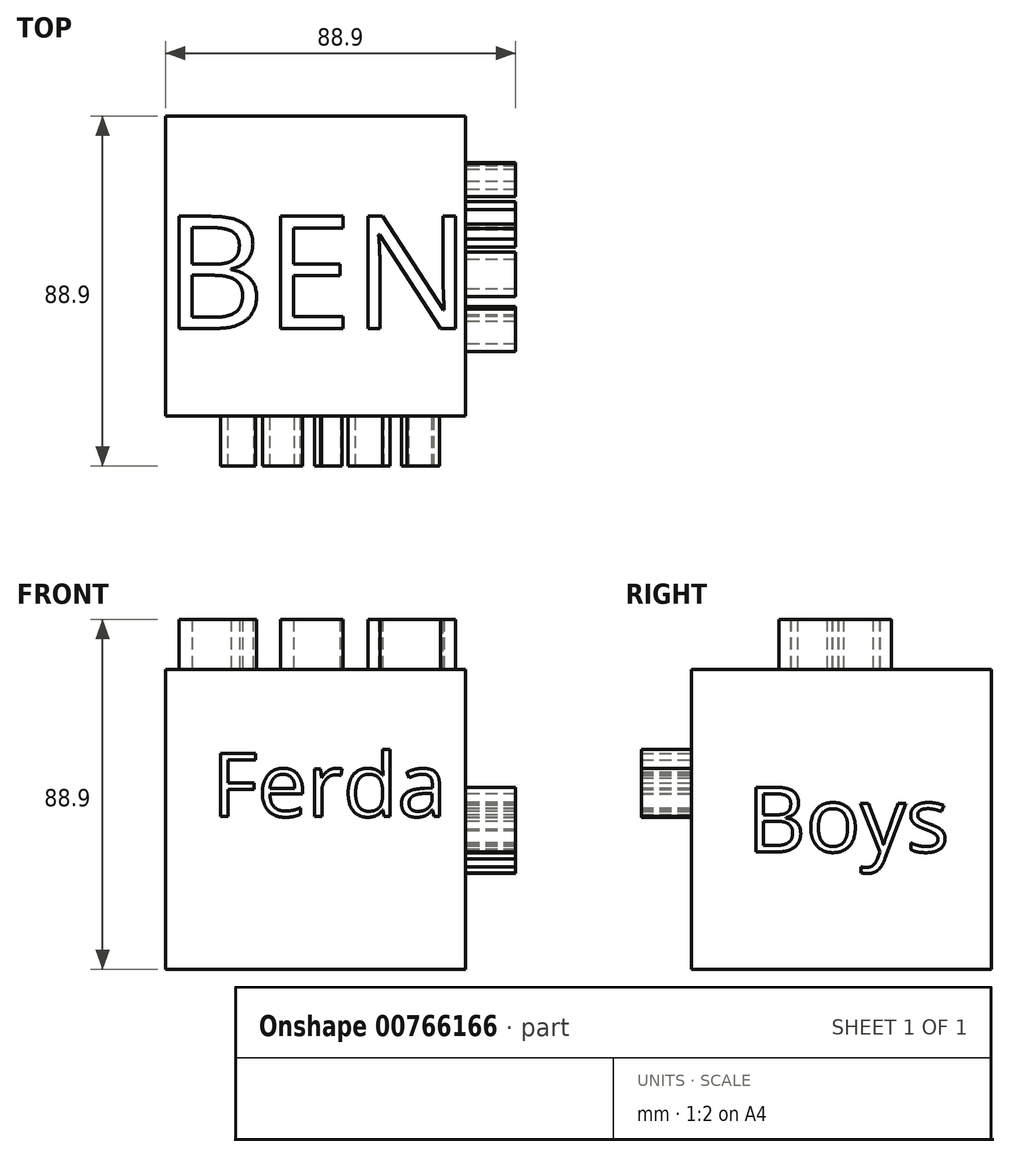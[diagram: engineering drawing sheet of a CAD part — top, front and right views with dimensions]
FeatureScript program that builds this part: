
annotation { "Feature Type Name" : "Feature", "Feature Type Description" : "" }
export const myFeature = defineFeature(function(context is Context, id is Id, definition is map)
    precondition{}
    {
        {
            var Q0;
            Q0=qCreatedBy(makeId("Front.planeOp"),FACE);
            var sketch = newSketch(context, id + "F0", { "sketchPlane" : qUnion([Q0])});
            skLineSegment(sketch, "E0.bottom", {"start": v(-41.32, 48.96) * mm, "end": v(34.88, 48.96) * mm});
            skLineSegment(sketch, "E0.top", {"start": v(-41.32, -27.24) * mm, "end": v(34.88, -27.24) * mm});
            skLineSegment(sketch, "E0.left", {"start": v(-41.32, 48.96) * mm, "end": v(-41.32, -27.24) * mm});
            skLineSegment(sketch, "E0.right", {"start": v(34.88, 48.96) * mm, "end": v(34.88, -27.24) * mm});
            skSolve(sketch);
        }
        {
            var Q0;
            Q0 = qSketchRegion(id + "F0", true);
            extrude(context, id + "F1", {"entities" : qUnion([Q0]), "depth" : 76.2 * mm, "offsetDistance" : 25.4 * mm});
        }
        {
            var Q0;
            Q0=makeQuery(id+"F1.opExtrude","SWEPT_FACE",FACE,{"disambiguationData":[OSD([sQuery(id+"F0.wireOp",EDGE,"E0.bottom")])]});
            var sketch = newSketch(context, id + "F2", { "sketchPlane" : qUnion([Q0])});
            skText(sketch, "E1", { "text": "BEN", "fontName": "OpenSans-Regular.ttf"});
            const initialGuessF2  = {"E1": [-0.04184, -0.05392, 1, 0, 0.0287]};
            skSetInitialGuess(sketch, initialGuessF2);
            skSolve(sketch);
        }
        {
            var Q0;
            Q0 = qSketchRegion(id + "F2", true);
            extrude(context, id + "F3", {"entities" : qUnion([Q0]), "operationType" : NewBodyOperationType.ADD, "depth" : 12.7 * mm, "offsetDistance" : 25.4 * mm});
        }
        {
            var Q0;
            Q0=makeQuery(id+"F1.opExtrude","CAP_FACE",FACE,{"disambiguationData":[OSD([sQuery(id+"F0.wireOp",EDGE,"E0.bottom"),sQuery(id+"F0.wireOp",EDGE,"E0.top"),sQuery(id+"F0.wireOp",EDGE,"E0.left"),sQuery(id+"F0.wireOp",EDGE,"E0.right")])],"isStart":false});
            var sketch = newSketch(context, id + "F4", { "sketchPlane" : qUnion([Q0])});
            skText(sketch, "E2", { "text": "Ferda", "fontName": "OpenSans-Regular.ttf"});
            const initialGuessF4  = {"E2": [-0.02958, 0.01162, 1, 0, 0.01618]};
            skSetInitialGuess(sketch, initialGuessF4);
            skSolve(sketch);
        }
        {
            var Q0;
            Q0 = qSketchRegion(id + "F4", true);
            extrude(context, id + "F5", {"entities" : qUnion([Q0]), "operationType" : NewBodyOperationType.ADD, "depth" : 12.7 * mm, "offsetDistance" : 25.4 * mm});
        }
        {
            var Q0;
            Q0=makeQuery(id+"F1.opExtrude","SWEPT_FACE",FACE,{"disambiguationData":[OSD([sQuery(id+"F0.wireOp",EDGE,"E0.right")])]});
            var sketch = newSketch(context, id + "F6", { "sketchPlane" : qUnion([Q0])});
            skText(sketch, "E3", { "text": "Boys", "fontName": "OpenSans-Regular.ttf"});
            const initialGuessF6  = {"E3": [-0.06208, 0.00264, 1, 0, 0.01656]};
            skSetInitialGuess(sketch, initialGuessF6);
            skSolve(sketch);
        }
        {
            var Q0;
            Q0 = qSketchRegion(id + "F6", true);
            extrude(context, id + "F7", {"entities" : qUnion([Q0]), "operationType" : NewBodyOperationType.ADD, "depth" : 12.7 * mm, "offsetDistance" : 25.4 * mm});
        }
    });
